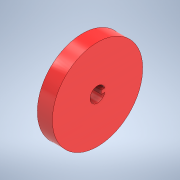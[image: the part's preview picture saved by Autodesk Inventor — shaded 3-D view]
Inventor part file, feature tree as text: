
AUTODESK INVENTOR PART (.ipt)
format: ipt  version: 2021 (Build 250183000, 183)  size: 117,248 bytes
history: native  units: in
note: dims shown in document units (in); Inventor stores cm internally (conversion verified against a paired STEP export)
features: other x4, extrude x2, sketch x2, plane x1, reference x1
ambient origin geometry x8: Origin, YZ Plane, XZ Plane, XY Plane, X Axis, Y Axis, Z Axis, Center Point
bodies: Solid1 (feature_tree)
feature tree (10):
  plane  "Work Plane1"
  extrude  "Extrusion1"  Depth=1.0in TaperAngle=0.0deg
  extrude  "Extrusion3"  Depth=0.5in
  sketch  "Sketch1"  dims[d0=6.0in d1=1.0in d2=0.0in]
  reference  "Reference1"
  sketch  "Sketch4"  dims[d7=0.25in d8=0.5in d9=1.0in d10=0.0in]
  parser-record x1  (decoder bookkeeping rows leaked as tree rows — omitted from the tree; the rows remain in map.json)
  other  "Clutch02.iam"
  other  "tubeBracketV02:1"
  other  "clutch02-forkBase:1"
note: 1 file-system path scrubbed to <path> (originals preserved in map.json)
